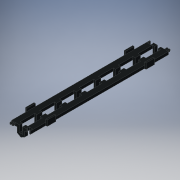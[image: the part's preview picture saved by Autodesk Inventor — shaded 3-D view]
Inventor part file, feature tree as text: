
AUTODESK INVENTOR PART (.ipt)
format: ipt  version: 2019 (Build 230136000, 136)  size: 314,880 bytes
history: native  units: mm
features: extrude x16, sketch x16, other x7
ambient origin geometry x8: Origin, YZ Plane, XZ Plane, XY Plane, X Axis, Y Axis, Z Axis, Center Point
bodies: Solid1 (feature_tree)
feature tree (39):
  extrude  "Extrusion1"  Depth=25.0mm TaperAngle=0.0deg
  extrude  "Extrusion2"  Depth=25.0mm TaperAngle=0.0deg
  extrude  "Extrusion3"  Depth=25.0mm TaperAngle=0.0deg
  extrude  "Extrusion4"  Depth=25.0mm TaperAngle=0.0deg
  extrude  "Extrusion5"  Depth=2.7mm TaperAngle=0.0deg
  extrude  "Extrusion6"  Depth=6.0mm TaperAngle=0.0deg
  extrude  "Extrusion7"  Depth=2.75mm TaperAngle=0.0deg
  extrude  "Extrusion8"  Depth=15.4mm TaperAngle=0.0deg
  extrude  "Extrusion9"  [1 undecoded]
  extrude  "Extrusion10"  [1 undecoded]
  extrude  "Extrusion11"  [1 undecoded]
  extrude  "Extrusion12"  [1 undecoded]
  extrude  "Extrusion13"  [1 undecoded]
  extrude  "Extrusion14"  [1 undecoded]
  extrude  "Extrusion15"  [1 undecoded]
  extrude  "Extrusion16"  [1 undecoded]
  other  "p1_XY"
  other  "p1_YZ"
  other  "p1_ZX"
  other  "p1_X"
  other  "p1_Y"
  other  "p1_Z"
  other  "p1_Center"
  sketch  "Sketch_1"  dims[d0=250.0mm d1=0.0mm d2=25.0mm d3=0.0mm]
  sketch  "Sketch_9"  dims[d28=15.4mm d29=0.0mm d30=15.4mm d31=0.0mm]
  sketch  "Sketch_2"  dims[d4=25.0mm d5=0.0mm d6=25.0mm d7=0.0mm]
  sketch  "Sketch_3"  dims[d8=25.0mm d9=0.0mm d10=25.0mm d11=0.0mm]
  sketch  "Sketch_4"  dims[d12=25.0mm d13=0.0mm d14=25.0mm d15=0.0mm]
  sketch  "Sketch_5"  dims[d16=2.7mm d17=0.0mm d18=2.7mm d19=0.0mm]
  sketch  "Sketch_6"  dims[d20=6.0mm d21=0.0mm d22=6.0mm d23=0.0mm]
  sketch  "Sketch_7"  dims[d24=2.75mm d25=0.0mm d26=2.75mm d27=0.0mm]
  sketch  "Sketch_10"  dims[d32=0.0mm]
  sketch  "Sketch_11"
  sketch  "Sketch_12"
  sketch  "Sketch_13"
  sketch  "Sketch_16"
  sketch  "Sketch_14"
  sketch  "Sketch_15"
  sketch  "Sketch_17"
note: 8 required parameter values undecoded (feature->parameter linkage not recoverable at this tier; creation-order binding heuristic only, values carry confidence <= 0.55)
